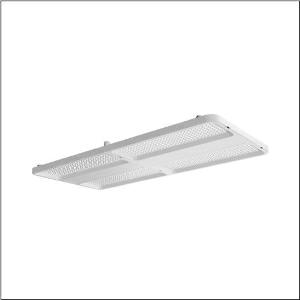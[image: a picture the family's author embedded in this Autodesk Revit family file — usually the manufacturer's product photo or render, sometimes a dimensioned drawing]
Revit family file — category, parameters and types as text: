
# Revit family: highbay_21_maxi_52hn11db5qda
name_source: partatom
category: Lighting Fixtures
units: mm (PartAtom-declared; Revit-internal decimal feet)

## family parameters
Cut with Voids When Loaded = No
Host = Face
Light Source = No
Part Type = Normal
Room Calculation Point = No
Round Connector Dimension = Use Diameter
Shared = No

## types (1)
- --- (1 x LED, 5680 lm, 31.4 W, 5000K)
    Apparent Load = 31 VA
    CIE Flux Codes = 89 97 99 100 100
    Color Rendering = 80
    Color Temperature = 5000K
    Default Elevation = 1800 mm
    Description = high bay luminaire Highbay 21 maxi; direct symmetric narrow distribution, light control with lens of PMMA; UGR ≤ 22 (X = 4H | Y = 8H | S = 0.25H | reflection values 70/50/20); luminous flux: 36.980lm; light colour: 850, colour temperature: 5000K, MacAdam ≤ 3 SDCM (initial), colour rendering: CRI > 80; luminous efficacy: 187,1lm/W; rated service life: 75.000h (L80) at AT= ta max; control: DALI 2; luminaire connection: terminal, 5-pole, max. 2.5mm² (cable entry for one cable, Ø 8.5..16mm); mains connection: 230..240V, AC/DC 0/50..60Hz; connected load: 197,7W; protection rating (complete): IP66; insulation class (complete): insulation class I (protective earthing); protection symbol: D; impact resistance: IK08; certification: CE, ENEC, VDE, UKCA; luminaire for central battery installations according to EN 60598-2-22, internal wiring halogen-free; luminaire LABS conformity tested according to VDMA 24364:2018-05; Suitable for use in the food industry according to the specifications of IFS-Food, HACCP and/or BRC; housing frame of high-performance plastic PA6, matt traffic white (RAL 9016); cover of PMMA; dimension (LxWxH): 946 x 442 x 72mm; permissible operating ambient temperature: -40..+60°C (reducing of maximum allowable ambient temperature of 5°C with ceiling mounting); packaging unit: 1 piece; (delivery without accessories; please order mounting accessories separately)
    Height = 72 mm  [stored 0.23622 ft]
    Lamp = 1 x LED
    Lamp Light Flux = 5680 lm
    Lamp Power = 31.4 W
    Lamp count = 1
    Length = 946 mm
    Luminous efficacy = 181 lm/W
    Manufacturer = Siteco
    ModVariant = No
    Model = 52HN11DB5QDA
    Mounting Place = Ceiling
    Mounting Type = Pendant
    Number of Poles = 1
    OnlyDefault = Yes
    Power Factor = 1
    Product Name = Highbay 21 maxi
    Product group = high bay luminaire
    ProductGroupID = 902
    Protection Class = Protection class I
    Protection Degree = IP 66
    RLX_Detail_Level = 1
    RLX_Emergency_Light_Flux = 0 lm
    RLX_Emergency_Type = 0
    RLX_Emergency_Type_DB = No
    RlxData = <blob elided: 128077 chars, md5=d4054e10>
    Socket = socket
    Standby Power = 0 W
    System Light Flux = 5680 lm
    System Power = 31 W
    Type Comments = : DC mode (central or group accumulator) initial emergency light level
    Type Image = l_1363244.jpg
    URL = http://relux.com
    VarID = @adj_003299
    Voltage = 0 V
    Weight = 0.00 kg
    Width = 442 mm

note: [stored X ft] marks values corroborated as IEEE doubles in the binary element streams (Revit-internal decimal feet)

## geometry (parser evidence)
native form markers: Blend x4, Sweep x11
no freeform markers — native parametric forms only
